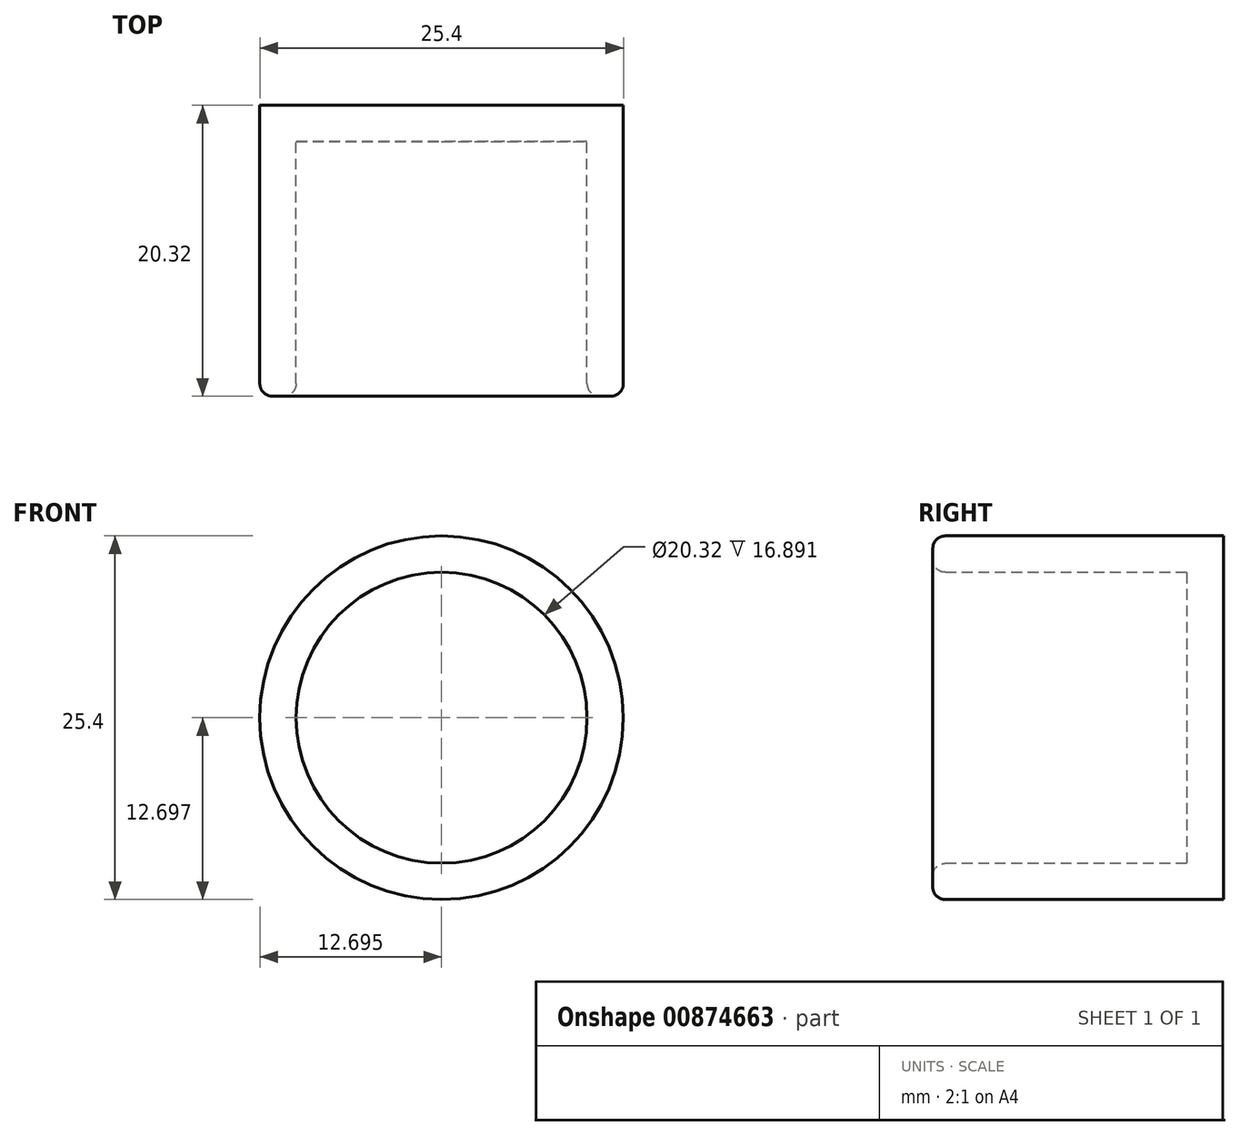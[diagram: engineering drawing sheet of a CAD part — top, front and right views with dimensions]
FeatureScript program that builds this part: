
annotation { "Feature Type Name" : "Feature", "Feature Type Description" : "" }
export const myFeature = defineFeature(function(context is Context, id is Id, definition is map)
    precondition{}
    {
        {
            var Q0;
            Q0=qCreatedBy(makeId("Front.planeOp"),FACE);
            var sketch = newSketch(context, id + "F0", { "sketchPlane" : qUnion([Q0])});
            skCircle(sketch, "E0", {"center": v(37.79, 47.89) * mm, "radius": 12.7 * mm});
            skSolve(sketch);
        }
        {
            var Q0;
            Q0=makeQuery(id+"F0.imprint","IMPRINT",FACE,{"disambiguationData":[TD([[makeQuery(id+"F0.imprint","IMPRINT",EDGE,{"derivedFrom":sQuery(id+"F0.wireOp",EDGE,"E0")}),1.0]])]});
            extrude(context, id + "F1", {"entities" : qUnion([Q0]), "depth" : 20.32 * mm, "offsetDistance" : 25.4 * mm});
        }
        {
            var Q0;
            Q0=makeQuery(id+"F1.opExtrude","CAP_FACE",FACE,{"disambiguationData":[OSD([sQuery(id+"F0.wireOp",EDGE,"E0")])],"isStart":false});
            shell(context, id + "F2", {"entities" : qUnion([Q0]), "thickness" : 2.54 * mm});
        }
        {
            var Q0;
            Q0=makeQuery(id+"F1.opExtrude","CAP_EDGE",EDGE,{"disambiguationData":[OSD([sQuery(id+"F0.wireOp",EDGE,"E0")])],"isStart":false});
            var Q1;
            {var subQ0=sQuery(id+"F0.wireOp",EDGE,"E0");Q1=makeQuery(id+"F2.opShell","OFFSET_EDGE",EDGE,{"disambiguationData":[OSD([subQ0]),TDD([makeQuery(id+"F1.opExtrude","CAP_EDGE",EDGE,{"disambiguationData":[OSD([subQ0])],"isStart":false})])]});}
            fillet(context, id + "F3", {"entities" : qUnion([Q0, Q1]), "radius" : 0.89 * mm, "tangentPropagation" : true, "allowEdgeOverflow" : false});
        }
    });
